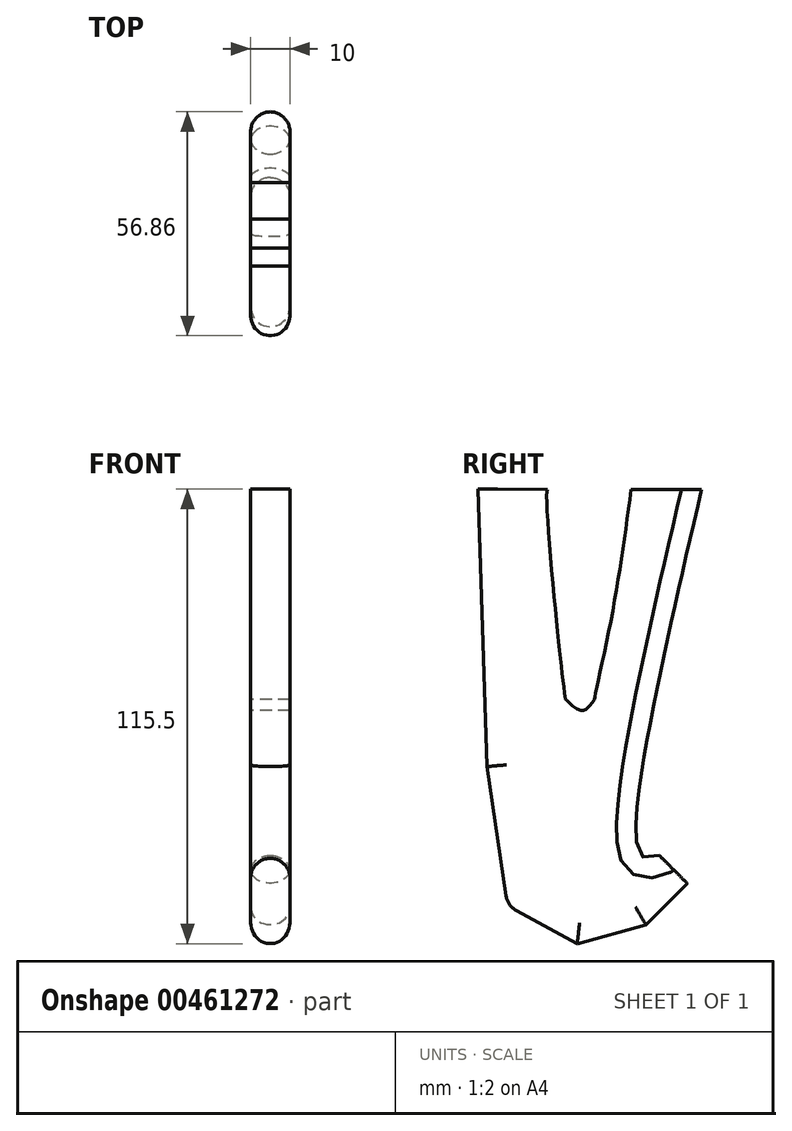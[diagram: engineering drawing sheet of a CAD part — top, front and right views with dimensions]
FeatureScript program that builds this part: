
annotation { "Feature Type Name" : "Feature", "Feature Type Description" : "" }
export const myFeature = defineFeature(function(context is Context, id is Id, definition is map)
    precondition{}
    {
        {
            var Q0;
            Q0=qCreatedBy(makeId("Top.planeOp"),FACE);
            var sketch = newSketch(context, id + "F0", { "sketchPlane" : qUnion([Q0])});
            skLineSegment(sketch, "E0.bottom", {"start": v(50, 50) * mm, "end": v(-50, 50) * mm});
            skLineSegment(sketch, "E0.top", {"start": v(50, -50) * mm, "end": v(-50, -50) * mm});
            skLineSegment(sketch, "E0.left", {"start": v(50, 50) * mm, "end": v(50, -50) * mm});
            skLineSegment(sketch, "E0.right", {"start": v(-50, 50) * mm, "end": v(-50, -50) * mm});
            skPoint(sketch, "E0.middle", {"position": v(0, 0) * mm});
            skSolve(sketch);
        }
        {
            var Q0;
            Q0=qCreatedBy(makeId("Right.planeOp"),FACE);
            var sketch = newSketch(context, id + "F1", { "sketchPlane" : qUnion([Q0])});
            skLineSegment(sketch, "E1", {"start": v(32.93, -92.93) * mm, "end": v(40, -100) * mm});
            skLineSegment(sketch, "E2", {"start": v(40, -100) * mm, "end": v(50, -100) * mm});
            skLineSegment(sketch, "E3", {"start": v(50, -100) * mm, "end": v(50, 0) * mm});
            skLineSegment(sketch, "E4", {"start": v(40, -100) * mm, "end": v(29.49, -110.51) * mm});
            skLineSegment(sketch, "E5", {"start": v(29.49, -110.51) * mm, "end": v(12.06, -115.35) * mm});
            skLineSegment(sketch, "E6", {"start": v(12.06, -115.35) * mm, "end": v(-5.63, -105.7) * mm});
            skLineSegment(sketch, "E7", {"start": v(-5.63, -105.7) * mm, "end": v(-10.9, -70.34) * mm});
            skLineSegment(sketch, "E8", {"start": v(-10.9, -70.34) * mm, "end": v(-13.2, 0.15) * mm});
            skFitSpline(sketch, "E9", {"points": [v(32.93, -92.93) * mm, v(28.21, -92.93) * mm, v(43.66, 0.05) * mm], "startDerivative": vector(-29.89, -10.4) * mm, "endDerivative": vector(37.17, 160.27) * mm});
            skLineSegment(sketch, "E10", {"start": v(43.66, 0.05) * mm, "end": v(-13.2, 0.15) * mm});
            skFitSpline(sketch, "E11", {"points": [v(25.73, 0.08) * mm, v(20.6, -33.3) * mm, v(16.42, -53.23) * mm, v(16.42, -53.42) * mm], "startDerivative": vector(-7.93, -60.16) * mm, "endDerivative": vector(0.5, -2.75) * mm});
            skFitSpline(sketch, "E12", {"points": [v(16.42, -53.23) * mm, v(13.39, -56.08) * mm, v(9.02, -53.23) * mm], "startDerivative": vector(-6, -8.73) * mm, "endDerivative": vector(-8.75, 8.41) * mm});
            skFitSpline(sketch, "E13", {"points": [v(9.02, -53.23) * mm, v(6.74, -32.92) * mm, v(4.46, 0.12) * mm, v(4.65, 0.12) * mm], "startDerivative": vector(-4.64, 37.52) * mm, "endDerivative": vector(5.01, -2.65) * mm});
            skSolve(sketch);
        }
        {
            var Q0;
            Q0=makeQuery(id+"F1.imprint","IMPRINT",FACE,{"disambiguationData":[TD([[makeQuery(id+"F1.imprint","IMPRINT",EDGE,{"derivedFrom":sQuery(id+"F1.wireOp",EDGE,"E1")}),-1.0]])]});
            extrude(context, id + "F2", {"entities" : qUnion([Q0]), "endBound" : BoundingType.SYMMETRIC, "depth" : 10 * mm});
        }
        {
            var Q0;
            Q0=makeQuery(id+"F2.opExtrude","CAP_EDGE",EDGE,{"disambiguationData":[OSD([sQuery(id+"F1.wireOp",EDGE,"E9")])],"isStart":false});
            var Q1;
            Q1=makeQuery(id+"F2.opExtrude","CAP_EDGE",EDGE,{"disambiguationData":[OSD([sQuery(id+"F1.wireOp",EDGE,"E4")])],"isStart":false});
            var Q2;
            Q2=makeQuery(id+"F2.opExtrude","CAP_EDGE",EDGE,{"disambiguationData":[OSD([sQuery(id+"F1.wireOp",EDGE,"E5")])],"isStart":false});
            var Q3;
            Q3=makeQuery(id+"F2.opExtrude","CAP_EDGE",EDGE,{"disambiguationData":[OSD([sQuery(id+"F1.wireOp",EDGE,"E7")])],"isStart":false});
            var Q4;
            Q4=makeQuery(id+"F2.opExtrude","CAP_EDGE",EDGE,{"disambiguationData":[OSD([sQuery(id+"F1.wireOp",EDGE,"E8")])],"isStart":false});
            var Q5;
            Q5=makeQuery(id+"F2.opExtrude","CAP_EDGE",EDGE,{"disambiguationData":[OSD([sQuery(id+"F1.wireOp",EDGE,"E6")])],"isStart":false});
            var Q6;
            Q6=makeQuery(id+"F2.opExtrude","CAP_EDGE",EDGE,{"disambiguationData":[OSD([sQuery(id+"F1.wireOp",EDGE,"E9")])],"isStart":true});
            var Q7;
            Q7=makeQuery(id+"F2.opExtrude","CAP_EDGE",EDGE,{"disambiguationData":[OSD([sQuery(id+"F1.wireOp",EDGE,"E4")])],"isStart":true});
            var Q8;
            Q8=makeQuery(id+"F2.opExtrude","CAP_EDGE",EDGE,{"disambiguationData":[OSD([sQuery(id+"F1.wireOp",EDGE,"E5")])],"isStart":true});
            var Q9;
            Q9=makeQuery(id+"F2.opExtrude","SWEPT_EDGE",EDGE,{"disambiguationData":[OSD([sQuery(id+"F1.wireOp",EDGE,"E6"),sQuery(id+"F1.wireOp",EDGE,"E7")])]});
            var Q10;
            Q10=makeQuery(id+"F2.opExtrude","CAP_EDGE",EDGE,{"disambiguationData":[OSD([sQuery(id+"F1.wireOp",EDGE,"E7")])],"isStart":true});
            var Q11;
            Q11=makeQuery(id+"F2.opExtrude","CAP_EDGE",EDGE,{"disambiguationData":[OSD([sQuery(id+"F1.wireOp",EDGE,"E8")])],"isStart":true});
            var Q12;
            Q12=makeQuery(id+"F2.opExtrude","CAP_EDGE",EDGE,{"disambiguationData":[OSD([sQuery(id+"F1.wireOp",EDGE,"E6")])],"isStart":true});
            fillet(context, id + "F3", {"entities" : qUnion([Q0, Q1, Q2, Q3, Q4, Q5, Q6, Q7, Q8, Q9, Q10, Q11, Q12]), "radius" : 5 * mm, "tangentPropagation" : true, "allowEdgeOverflow" : false});
        }
    });
